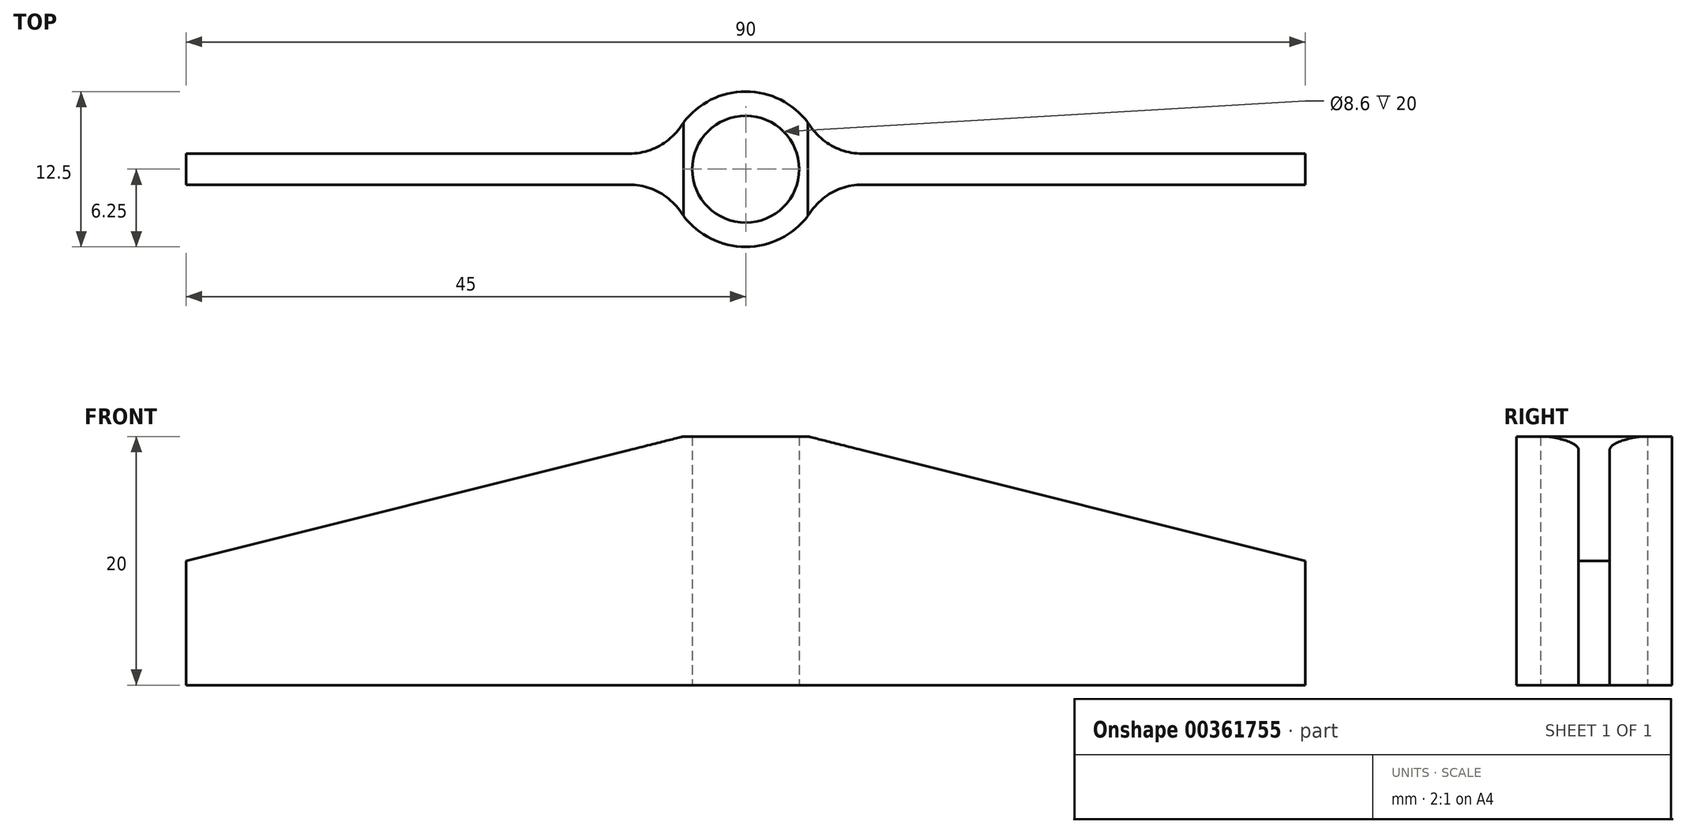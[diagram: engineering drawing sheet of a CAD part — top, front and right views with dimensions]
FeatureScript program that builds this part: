
annotation { "Feature Type Name" : "Feature", "Feature Type Description" : "" }
export const myFeature = defineFeature(function(context is Context, id is Id, definition is map)
    precondition{}
    {
        {
            var Q0;
            Q0=qCreatedBy(makeId("Top.planeOp"),FACE);
            var sketch = newSketch(context, id + "F0", { "sketchPlane" : qUnion([Q0])});
            skArc(sketch, "E0", {"start": v(-6.12, -1.25) * mm, "mid": v(0, -6.25) * mm, "end": v(6.12, -1.25) * mm});
            skCircle(sketch, "E1", {"center": v(0, 0) * mm, "radius": 4.3 * mm});
            skLineSegment(sketch, "E2", {"start": v(-6.12, 1.25) * mm, "end": v(-45, 1.25) * mm});
            skLineSegment(sketch, "E3", {"start": v(-45, 1.25) * mm, "end": v(-45, -1.25) * mm});
            skLineSegment(sketch, "E4", {"start": v(-45, -1.25) * mm, "end": v(-6.12, -1.25) * mm});
            skLineSegment(sketch, "E5.1.0", {"start": v(45, 1.25) * mm, "end": v(6.12, 1.25) * mm});
            skLineSegment(sketch, "E5.1.1", {"start": v(6.12, -1.25) * mm, "end": v(45, -1.25) * mm});
            skLineSegment(sketch, "E5.1.2", {"start": v(45, -1.25) * mm, "end": v(45, 1.25) * mm});
            skArc(sketch, "E6.trimOffspring", {"start": v(6.12, 1.25) * mm, "mid": v(0, 6.25) * mm, "end": v(-6.12, 1.25) * mm});
            skSolve(sketch);
        }
        {
            var Q0;
            Q0=makeQuery(id+"F0.imprint","IMPRINT",FACE,{"disambiguationData":[TD([[makeQuery(id+"F0.imprint","IMPRINT",EDGE,{"derivedFrom":sQuery(id+"F0.wireOp",EDGE,"E0")}),1.0]])]});
            extrude(context, id + "F1", {"entities" : qUnion([Q0]), "depth" : 20 * mm, "offsetDistance" : 25 * mm});
        }
        {
            var Q0;
            Q0=makeQuery(id+"F1.opExtrude","SWEPT_EDGE",EDGE,{"disambiguationData":[OSD([sQuery(id+"F0.wireOp",EDGE,"E0"),sQuery(id+"F0.wireOp",EDGE,"E4")])]});
            var Q1;
            Q1=makeQuery(id+"F1.opExtrude","SWEPT_EDGE",EDGE,{"disambiguationData":[OSD([sQuery(id+"F0.wireOp",EDGE,"E0"),sQuery(id+"F0.wireOp",EDGE,"E5.1.1")])]});
            var Q2;
            Q2=makeQuery(id+"F1.opExtrude","SWEPT_EDGE",EDGE,{"disambiguationData":[OSD([sQuery(id+"F0.wireOp",EDGE,"E2"),sQuery(id+"F0.wireOp",EDGE,"E6.trimOffspring")])]});
            var Q3;
            Q3=makeQuery(id+"F1.opExtrude","SWEPT_EDGE",EDGE,{"disambiguationData":[OSD([sQuery(id+"F0.wireOp",EDGE,"E5.1.0"),sQuery(id+"F0.wireOp",EDGE,"E6.trimOffspring")])]});
            fillet(context, id + "F2", {"entities" : qUnion([Q0, Q1, Q2, Q3]), "radius" : 5 * mm, "tangentPropagation" : true, "allowEdgeOverflow" : false});
        }
        {
            var Q0;
            Q0=makeQuery(id+"F1.opExtrude","CAP_EDGE",EDGE,{"disambiguationData":[OSD([sQuery(id+"F0.wireOp",EDGE,"E3")])],"isStart":false});
            var Q1;
            Q1=makeQuery(id+"F1.opExtrude","CAP_EDGE",EDGE,{"disambiguationData":[OSD([sQuery(id+"F0.wireOp",EDGE,"E5.1.2")])],"isStart":false});
            chamfer(context, id + "F3", {"entities" : qUnion([Q0, Q1]), "chamferType" : ChamferType.TWO_OFFSETS, "width1" : 40 * mm, "oppositeDirection" : false, "width2" : 10 * mm, "tangentPropagation" : true});
        }
    });
